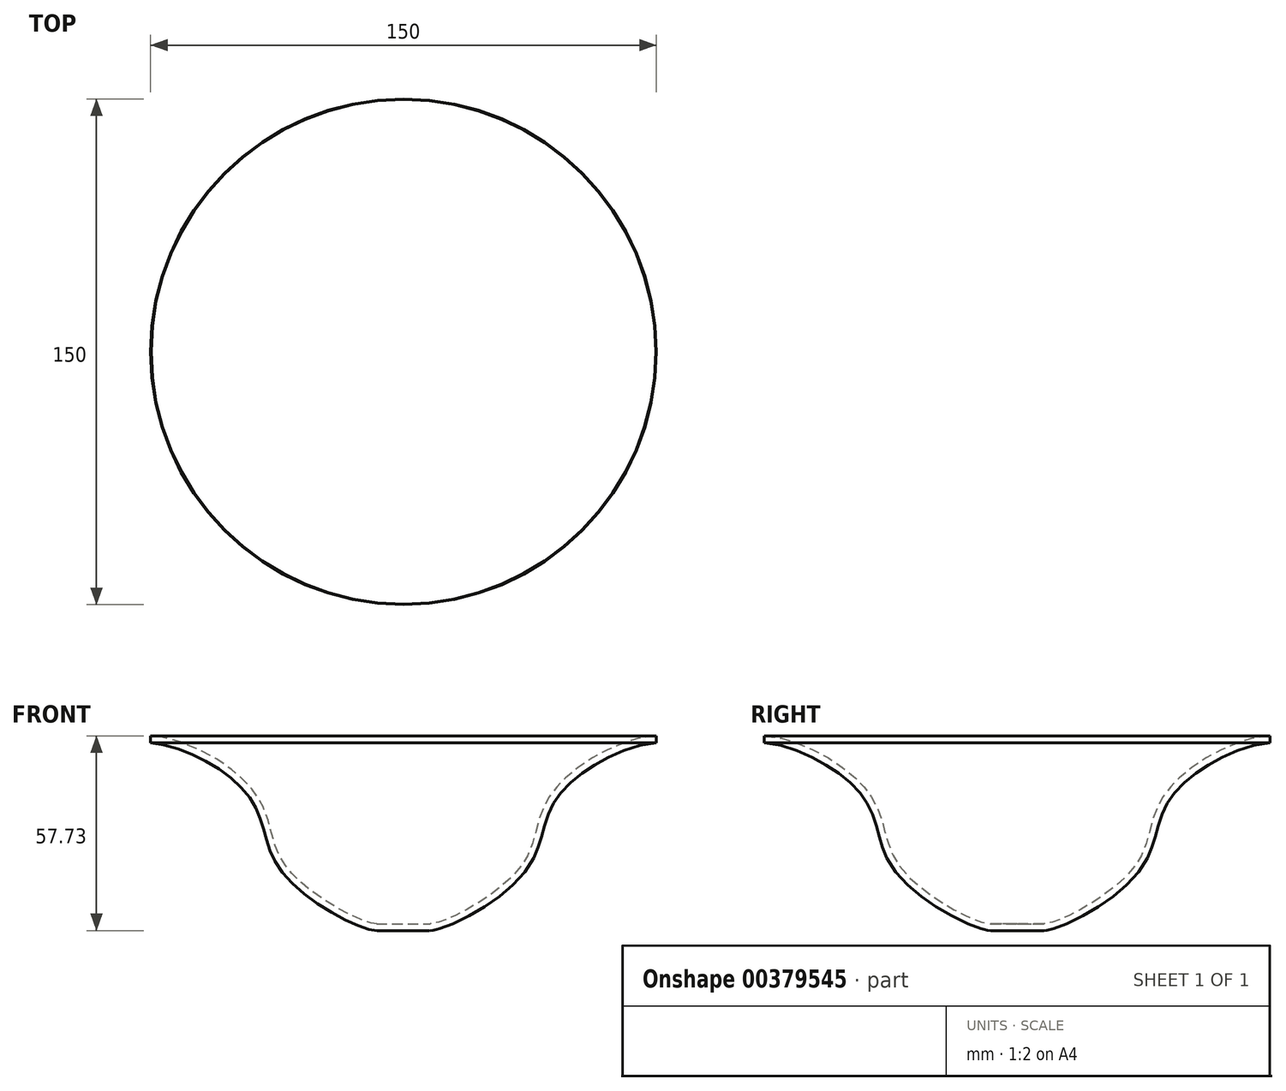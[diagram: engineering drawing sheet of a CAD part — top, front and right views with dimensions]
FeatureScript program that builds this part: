
annotation { "Feature Type Name" : "Feature", "Feature Type Description" : "" }
export const myFeature = defineFeature(function(context is Context, id is Id, definition is map)
    precondition{}
    {
        {
            var Q0;
            Q0=qCreatedBy(makeId("Front.planeOp"),FACE);
            var sketch = newSketch(context, id + "F0", { "sketchPlane" : qUnion([Q0])});
            skLineSegment(sketch, "E0", {"start": v(0, 0) * mm, "end": v(0, 164.23) * mm, "construction": true});
            skLineSegment(sketch, "E1", {"start": v(0, 0) * mm, "end": v(-7.86, 0) * mm});
            skLineSegment(sketch, "E2", {"start": v(-75, 55.74) * mm, "end": v(0, 55.74) * mm, "construction": true});
            skFitSpline(sketch, "E3", {"points": [v(-7.86, 0) * mm, v(-36.14, 17.5) * mm, v(-45.14, 38.85) * mm, v(-75, 55.74) * mm], "startDerivative": vector(-44.22, 0) * mm, "endDerivative": vector(-87.4, 7.71) * mm});
            skLineSegment(sketch, "E4", {"start": v(-75, 55.74) * mm, "end": v(-75, 57.73) * mm});
            skLineSegment(sketch, "E5", {"start": v(-74.82, 57.73) * mm, "end": v(-75, 57.73) * mm});
            skLineSegment(sketch, "E6.0", {"start": v(0, 2) * mm, "end": v(-7.86, 2) * mm});
            skLineSegment(sketch, "E7", {"start": v(0, 2) * mm, "end": v(0, 0) * mm});
            skFitSpline(sketch, "E8.0", {"points": [v(-7.86, 2) * mm, v(-7.99, 2) * mm, v(-8.33, 2.02) * mm, v(-9.29, 2.18) * mm, v(-10.87, 2.62) * mm, v(-13.19, 3.5) * mm, v(-15.8, 4.7) * mm, v(-18.62, 6.16) * mm, v(-21.53, 7.85) * mm, v(-24.45, 9.73) * mm, v(-27.27, 11.75) * mm, v(-29.9, 13.88) * mm, v(-32.27, 16.06) * mm, v(-33.92, 17.88) * mm, v(-35, 19.3) * mm, v(-35.96, 20.72) * mm, v(-36.92, 22.5) * mm, v(-37.82, 24.64) * mm, v(-38.54, 26.83) * mm, v(-39.37, 29.82) * mm, v(-40.18, 32.92) * mm, v(-41.36, 36.11) * mm, v(-42.33, 38.12) * mm, v(-43.3, 39.73) * mm, v(-44.4, 41.32) * mm, v(-46.01, 43.25) * mm, v(-48.25, 45.46) * mm, v(-51.59, 48.25) * mm, v(-56.3, 51.42) * mm, v(-62.46, 54.53) * mm, v(-68.77, 56.77) * mm, v(-72.86, 57.56) * mm, v(-74.82, 57.73) * mm]});
            skLineSegment(sketch, "E9", {"start": v(-7.86, 2) * mm, "end": v(-7.98, 2) * mm});
            skSolve(sketch);
        }
        {
            var Q0;
            Q0=makeQuery(id+"F0.imprint","IMPRINT",FACE,{"disambiguationData":[TD([[makeQuery(id+"F0.imprint","IMPRINT",EDGE,{"derivedFrom":sQuery(id+"F0.wireOp",EDGE,"E1")}),-1.0]])]});
            var Q1;
            Q1=sQuery(id+"F0.wireOp",EDGE,"E0");
            revolve(context, id + "F1", {"entities" : qUnion([Q0]), "axis" : qUnion([Q1]), "revolveType" : RevolveType.FULL});
        }
    });
